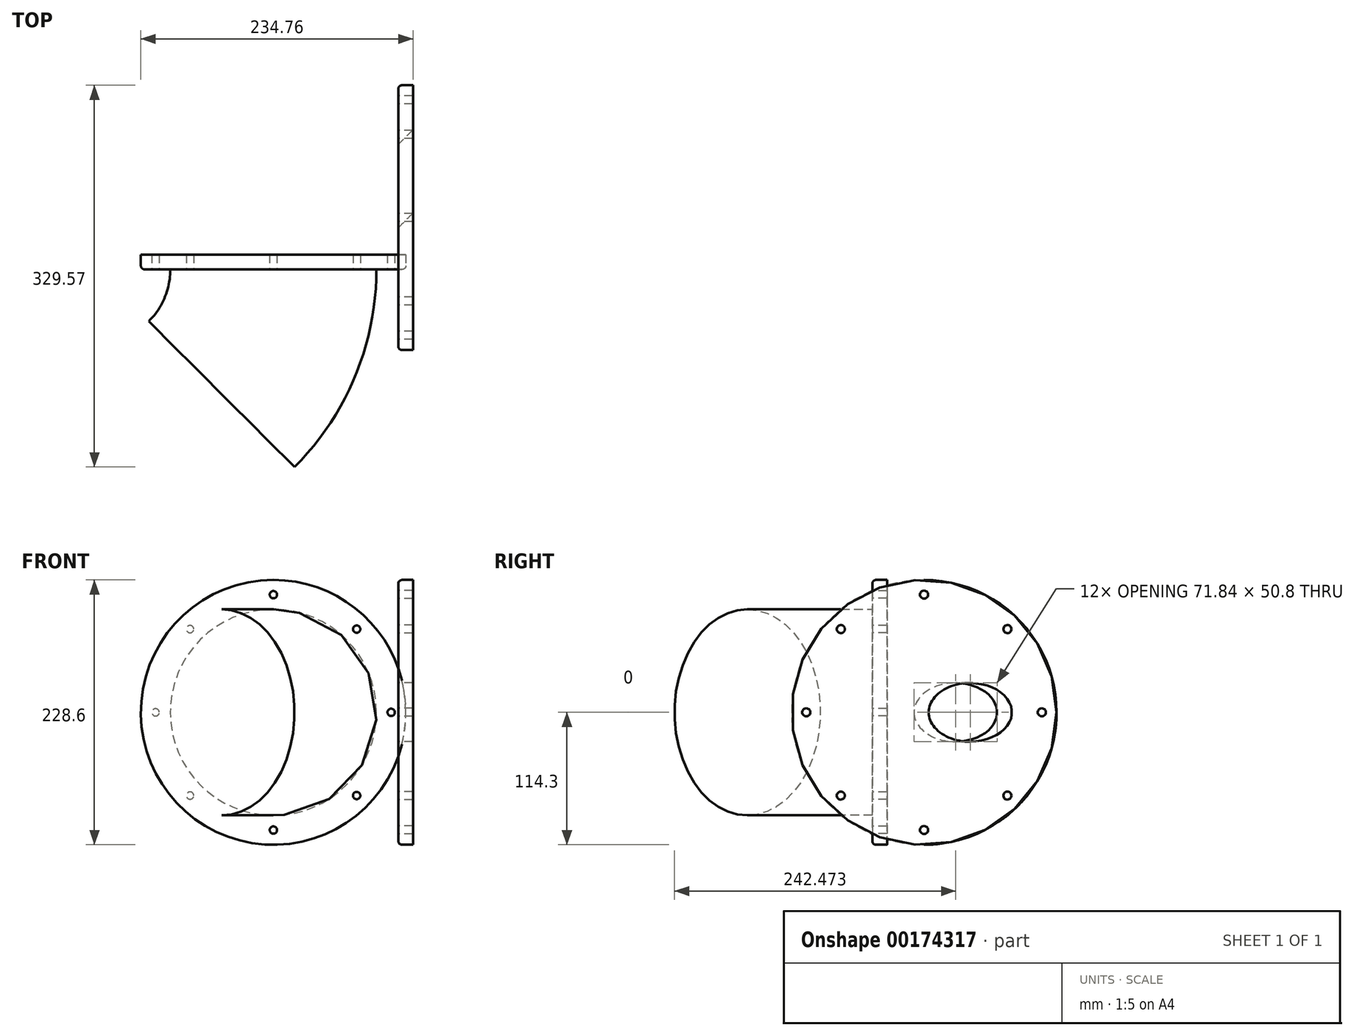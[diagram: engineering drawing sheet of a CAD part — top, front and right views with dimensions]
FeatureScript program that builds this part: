
annotation { "Feature Type Name" : "Feature", "Feature Type Description" : "" }
export const myFeature = defineFeature(function(context is Context, id is Id, definition is map)
    precondition{}
    {
        {
            var Q0;
            Q0=qCreatedBy(makeId("Front.planeOp"),FACE);
            var sketch = newSketch(context, id + "F0", { "sketchPlane" : qUnion([Q0])});
            skCircle(sketch, "E0", {"center": v(0, 0) * mm, "radius": 88.9 * mm});
            skSolve(sketch);
        }
        {
            var Q0;
            Q0=qCreatedBy(makeId("Top.planeOp"),FACE);
            var sketch = newSketch(context, id + "F1", { "sketchPlane" : qUnion([Q0])});
            skArc(sketch, "E1", {"start": v(-44.64, -107.76) * mm, "mid": v(-11.6, -58.32) * mm, "end": v(0, 0) * mm});
            skLineSegment(sketch, "E2", {"start": v(-152.4, 0) * mm, "end": v(-16.1, -136.3) * mm});
            skPoint(sketch, "E3.orphan", {"position": v(-151.86, -152.4) * mm});
            skSolve(sketch);
        }
        {
            var Q0;
            Q0=makeQuery(id+"F0.imprint","IMPRINT",FACE,{"disambiguationData":[TD([[makeQuery(id+"F0.imprint","IMPRINT",EDGE,{"derivedFrom":sQuery(id+"F0.wireOp",EDGE,"E0")}),1.0]])]});
            var Q1;
            Q1=sQuery(id+"F1.wireOp",EDGE,"E1");
            sweep(context, id + "F2", {"profiles" : qUnion([Q0]), "path" : qUnion([Q1])});
        }
        {
            var Q0;
            Q0=makeQuery(id+"F2.opSweep","CAP_FACE",FACE,{"disambiguationData":[OSD([sQuery(id+"F0.wireOp",EDGE,"E0"),sQuery(id+"F1.wireOp",VERTEX,"E1.end")])],"isStart":true});
            var sketch = newSketch(context, id + "F3", { "sketchPlane" : qUnion([Q0])});
            skCircle(sketch, "E4", {"center": v(0, 0) * mm, "radius": 114.3 * mm});
            skCircle(sketch, "E5", {"center": v(-101.6, 0) * mm, "radius": 3.18 * mm});
            skCircle(sketch, "E6.1.0", {"center": v(-71.84, -71.84) * mm, "radius": 3.18 * mm});
            skCircle(sketch, "E6.2.0", {"center": v(0, -101.6) * mm, "radius": 3.18 * mm});
            skCircle(sketch, "E6.3.0", {"center": v(71.84, -71.84) * mm, "radius": 3.18 * mm});
            skCircle(sketch, "E6.4.0", {"center": v(101.6, 0) * mm, "radius": 3.18 * mm});
            skCircle(sketch, "E6.5.0", {"center": v(71.84, 71.84) * mm, "radius": 3.18 * mm});
            skCircle(sketch, "E6.6.0", {"center": v(0, 101.6) * mm, "radius": 3.18 * mm});
            skCircle(sketch, "E6.7.0", {"center": v(-71.84, 71.84) * mm, "radius": 3.18 * mm});
            skSolve(sketch);
        }
        {
            var Q0;
            Q0 = qSketchRegion(id + "F3", true);
            extrude(context, id + "F4", {"entities" : qUnion([Q0]), "depth" : 12.7 * mm});
        }
        {
            var Q0;
            Q0=makeQuery(id+"F2.opSweep","CAP_FACE",FACE,{"disambiguationData":[OSD([sQuery(id+"F0.wireOp",EDGE,"E0"),sQuery(id+"F1.wireOp",VERTEX,"E1.start")])],"isStart":false});
            var sketch = newSketch(context, id + "F5", { "sketchPlane" : qUnion([Q0])});
            skCircle(sketch, "E7", {"center": v(44.64, 0) * mm, "radius": 114.3 * mm});
            skCircle(sketch, "E8", {"center": v(44.64, 101.6) * mm, "radius": 3.5 * mm});
            skCircle(sketch, "E9.1.0", {"center": v(-27.2, 71.84) * mm, "radius": 3.5 * mm});
            skCircle(sketch, "E9.2.0", {"center": v(-56.96, 0) * mm, "radius": 3.5 * mm});
            skCircle(sketch, "E9.3.0", {"center": v(-27.2, -71.84) * mm, "radius": 3.5 * mm});
            skCircle(sketch, "E9.4.0", {"center": v(44.64, -101.6) * mm, "radius": 3.5 * mm});
            skCircle(sketch, "E9.5.0", {"center": v(116.48, -71.84) * mm, "radius": 3.5 * mm});
            skCircle(sketch, "E9.6.0", {"center": v(146.24, 0) * mm, "radius": 3.5 * mm});
            skCircle(sketch, "E9.7.0", {"center": v(116.48, 71.84) * mm, "radius": 3.5 * mm});
            skSolve(sketch);
        }
        {
            var Q0;
            Q0 = qSketchRegion(id + "F5", true);
            extrude(context, id + "F6", {"entities" : qUnion([Q0]), "depth" : 12.7 * mm});
        }
        {
            var Q0;
            Q0=makeQuery(id+"F6.opExtrude","CAP_EDGE",EDGE,{"disambiguationData":[OSD([sQuery(id+"F5.wireOp",EDGE,"E7")])],"isStart":true});
            var Q1;
            Q1=makeQuery(id+"F4.opExtrude","CAP_EDGE",EDGE,{"disambiguationData":[OSD([sQuery(id+"F3.wireOp",EDGE,"E4")])],"isStart":true});
            fillet(context, id + "F7", {"entities" : qUnion([Q0, Q1]), "radius" : 3.17 * mm, "tangentPropagation" : true, "allowEdgeOverflow" : false});
        }
        {
            var Q0;
            Q0=qCreatedBy(makeId("Right.planeOp"),FACE);
            var sketch = newSketch(context, id + "F8", { "sketchPlane" : qUnion([Q0])});
            skLineSegment(sketch, "E10", {"start": v(0, 0) * mm, "end": v(0, 170.98) * mm});
            skSolve(sketch);
        }
        {
            var Q0;
            Q0=qCreatedBy(makeId("Front.planeOp"),FACE);
            var sketch = newSketch(context, id + "F9", { "sketchPlane" : qUnion([Q0])});
            skCircle(sketch, "E11", {"center": v(-25.4, 0) * mm, "radius": 25.4 * mm});
            skSolve(sketch);
        }
        {
            var Q0;
            Q0 = qSketchRegion(id + "F9", true);
            extrude(context, id + "F10", {"entities" : qUnion([Q0]), "depth" : 203.2 * mm});
        }
        {
            var Q0;
            Q0=makeQuery(id+"F10.opExtrude","SWEPT_BODY",BODY,{"disambiguationData":[OSD([sQuery(id+"F9.wireOp",EDGE,"E11")])]});
            transform(context, id + "F11", {"entities" : qUnion([Q0]), "transformType" : TransformType.TRANSLATION_3D, "dx" : 0 * mm, "dy" : 25.4 * mm, "dz" : 0 * mm, "makeCopy" : false});
        }
        {
            var Q0;
            Q0=makeQuery(id+"F10.opExtrude","SWEPT_BODY",BODY,{"disambiguationData":[OSD([sQuery(id+"F9.wireOp",EDGE,"E11")])]});
            var Q1;
            Q1=makeQuery(id+"F6.opExtrude","SWEPT_BODY",BODY,{"disambiguationData":[OSD([sQuery(id+"F5.wireOp",EDGE,"E7"),sQuery(id+"F5.wireOp",EDGE,"E8"),sQuery(id+"F5.wireOp",EDGE,"E9.1.0"),sQuery(id+"F5.wireOp",EDGE,"E9.2.0"),sQuery(id+"F5.wireOp",EDGE,"E9.3.0"),sQuery(id+"F5.wireOp",EDGE,"E9.4.0"),sQuery(id+"F5.wireOp",EDGE,"E9.5.0"),sQuery(id+"F5.wireOp",EDGE,"E9.6.0"),sQuery(id+"F5.wireOp",EDGE,"E9.7.0")])]});
            booleanBodies(context, id + "F12", {"operationType" : BooleanOperationType.SUBTRACTION, "tools" : qUnion([Q0]), "targets" : qUnion([Q1])});
        }
        {
            var Q0;
            Q0=makeQuery(id+"F6.opExtrude","SWEPT_BODY",BODY,{"disambiguationData":[OSD([sQuery(id+"F5.wireOp",EDGE,"E7"),sQuery(id+"F5.wireOp",EDGE,"E8"),sQuery(id+"F5.wireOp",EDGE,"E9.1.0"),sQuery(id+"F5.wireOp",EDGE,"E9.2.0"),sQuery(id+"F5.wireOp",EDGE,"E9.3.0"),sQuery(id+"F5.wireOp",EDGE,"E9.4.0"),sQuery(id+"F5.wireOp",EDGE,"E9.5.0"),sQuery(id+"F5.wireOp",EDGE,"E9.6.0"),sQuery(id+"F5.wireOp",EDGE,"E9.7.0")])]});
            var Q1;
            Q1=sQuery(id+"F8.wireOp",EDGE,"E10");
            transform(context, id + "F13", {"entities" : qUnion([Q0]), "transformType" : TransformType.ROTATION, "transformAxis" : qUnion([Q1]), "angle" : 135 * degree, "makeCopy" : false});
        }
    });
